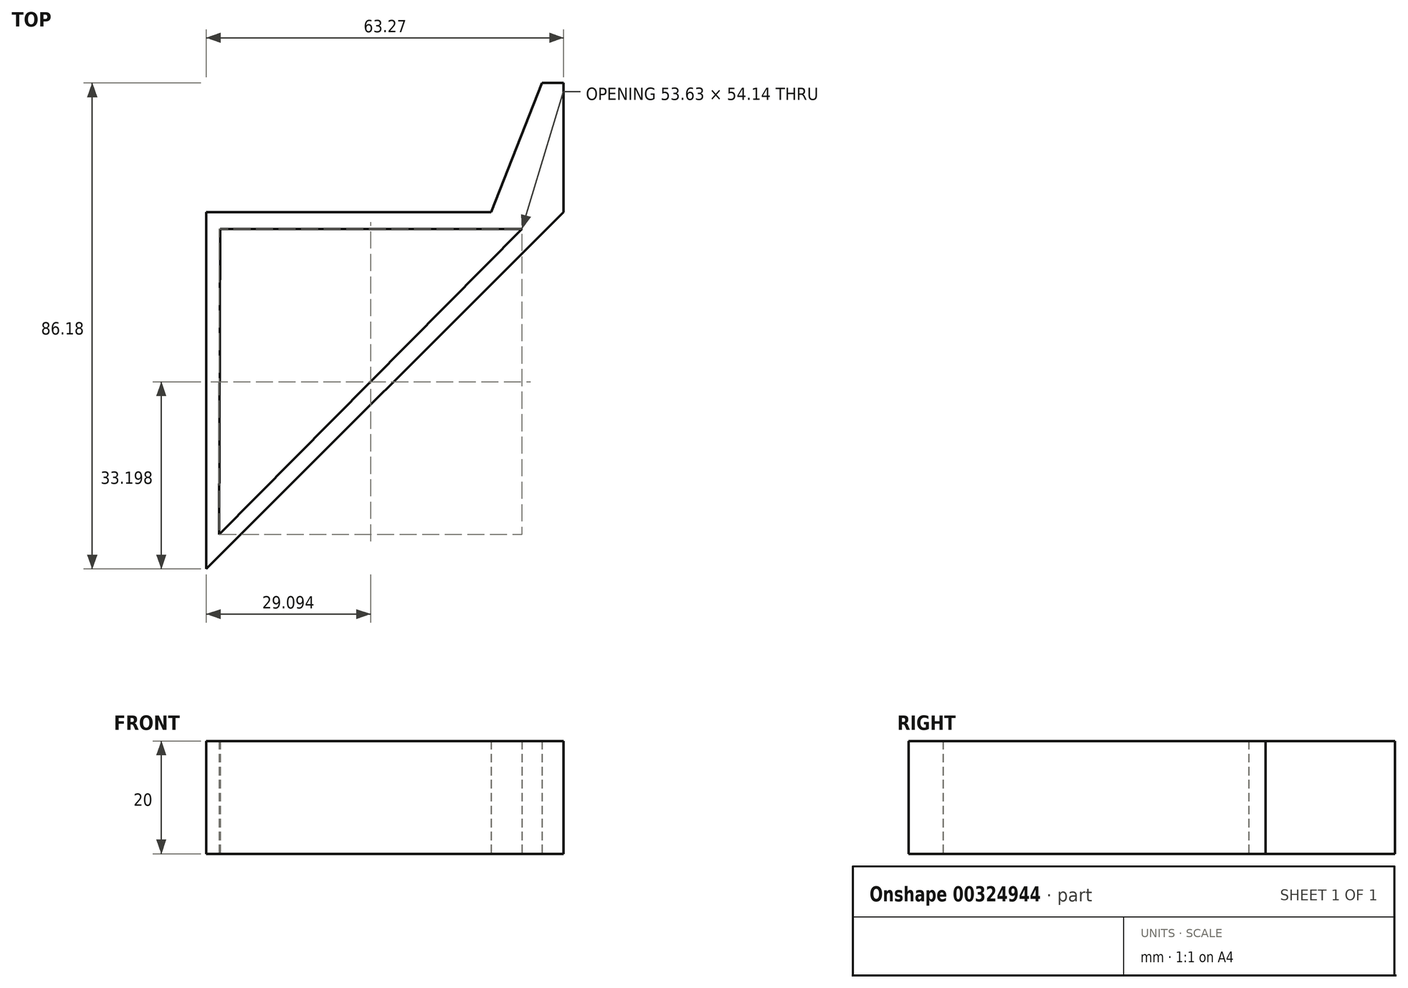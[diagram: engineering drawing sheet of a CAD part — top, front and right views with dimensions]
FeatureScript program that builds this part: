
annotation { "Feature Type Name" : "Feature", "Feature Type Description" : "" }
export const myFeature = defineFeature(function(context is Context, id is Id, definition is map)
    precondition{}
    {
        {
            var Q0;
            Q0=qCreatedBy(makeId("Top.planeOp"),FACE);
            var sketch = newSketch(context, id + "F0", { "sketchPlane" : qUnion([Q0])});
            skLineSegment(sketch, "E0", {"start": v(23.9, 39.48) * mm, "end": v(-26.55, 39.48) * mm});
            skLineSegment(sketch, "E1", {"start": v(-26.55, 39.48) * mm, "end": v(-26.55, -23.8) * mm});
            skLineSegment(sketch, "E2", {"start": v(-26.55, -23.8) * mm, "end": v(36.72, 39.48) * mm});
            skLineSegment(sketch, "E3", {"start": v(-24.1, 36.48) * mm, "end": v(29.36, 36.48) * mm});
            skLineSegment(sketch, "E4", {"start": v(29.36, 36.48) * mm, "end": v(-24.27, -17.66) * mm});
            skLineSegment(sketch, "E5", {"start": v(-24.27, -17.66) * mm, "end": v(-24.1, 36.48) * mm});
            skLineSegment(sketch, "E6", {"start": v(36.72, 39.48) * mm, "end": v(36.72, 62.39) * mm});
            skLineSegment(sketch, "E7", {"start": v(36.72, 62.39) * mm, "end": v(32.9, 62.39) * mm});
            skLineSegment(sketch, "E8", {"start": v(32.9, 62.39) * mm, "end": v(23.9, 39.48) * mm});
            skSolve(sketch);
        }
        {
            var Q0;
            Q0=makeQuery(id+"F0.imprint","IMPRINT",FACE,{"disambiguationData":[TD([[makeQuery(id+"F0.imprint","IMPRINT",EDGE,{"derivedFrom":sQuery(id+"F0.wireOp",EDGE,"E0")}),1.0]])]});
            extrude(context, id + "F1", {"entities" : qUnion([Q0]), "depth" : 20 * mm});
        }
    });
